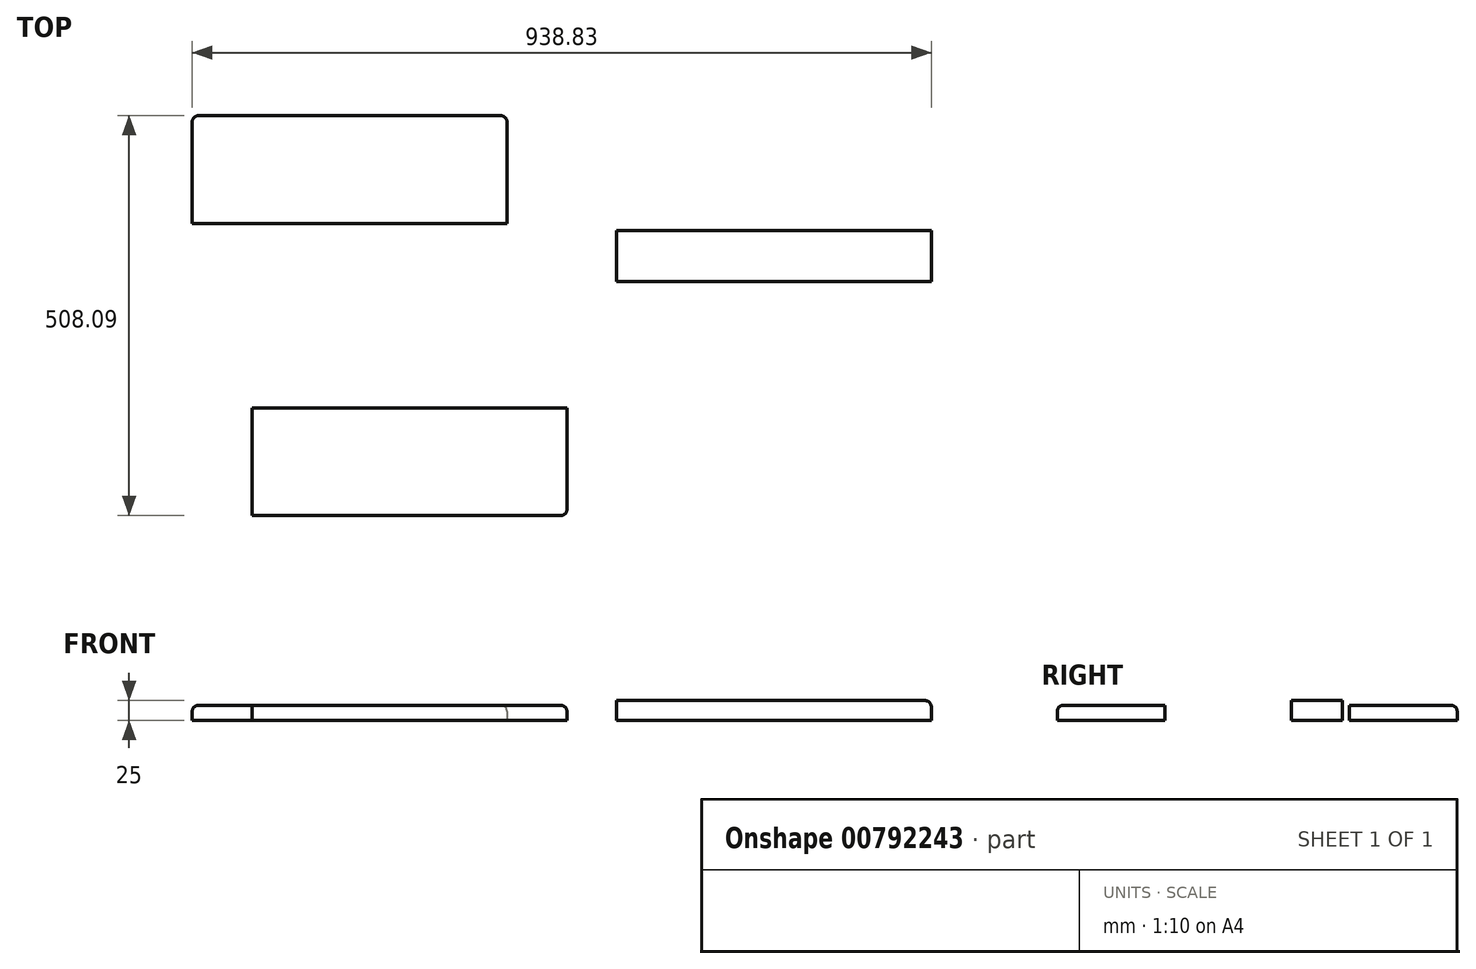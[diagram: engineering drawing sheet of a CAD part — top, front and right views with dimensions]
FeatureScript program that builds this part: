
annotation { "Feature Type Name" : "Feature", "Feature Type Description" : "" }
export const myFeature = defineFeature(function(context is Context, id is Id, definition is map)
    precondition{}
    {
        {
            var Q0;
            Q0=qCreatedBy(makeId("Top.planeOp"),FACE);
            var sketch = newSketch(context, id + "F0", { "sketchPlane" : qUnion([Q0])});
            skLineSegment(sketch, "E0.bottom", {"start": v(0.43, 41.34) * mm, "end": v(-399.57, 41.34) * mm});
            skLineSegment(sketch, "E0.top", {"start": v(0.43, 178.34) * mm, "end": v(-399.57, 178.34) * mm});
            skLineSegment(sketch, "E0.left", {"start": v(0.43, 41.34) * mm, "end": v(0.43, 178.34) * mm});
            skLineSegment(sketch, "E0.right", {"start": v(-399.57, 41.34) * mm, "end": v(-399.57, 178.34) * mm});
            skPoint(sketch, "E0.middle", {"position": v(-199.57, 109.84) * mm});
            skSolve(sketch);
        }
        {
            var Q0;
            Q0=qCreatedBy(makeId("Top.planeOp"),FACE);
            var sketch = newSketch(context, id + "F1", { "sketchPlane" : qUnion([Q0])});
            skLineSegment(sketch, "E1.bottom", {"start": v(76.53, -329.75) * mm, "end": v(-323.47, -329.75) * mm});
            skLineSegment(sketch, "E1.top", {"start": v(76.53, -192.75) * mm, "end": v(-323.47, -192.75) * mm});
            skLineSegment(sketch, "E1.left", {"start": v(76.53, -329.75) * mm, "end": v(76.53, -192.75) * mm});
            skLineSegment(sketch, "E1.right", {"start": v(-323.47, -329.75) * mm, "end": v(-323.47, -192.75) * mm});
            skPoint(sketch, "E1.middle", {"position": v(-123.47, -261.25) * mm});
            skSolve(sketch);
        }
        {
            var Q0;
            Q0=qCreatedBy(makeId("Top.planeOp"),FACE);
            var sketch = newSketch(context, id + "F2", { "sketchPlane" : qUnion([Q0])});
            skLineSegment(sketch, "E2.bottom", {"start": v(539.26, 32.5) * mm, "end": v(139.26, 32.5) * mm});
            skLineSegment(sketch, "E2.top", {"start": v(539.26, -32.5) * mm, "end": v(139.26, -32.5) * mm});
            skLineSegment(sketch, "E2.left", {"start": v(539.26, 32.5) * mm, "end": v(539.26, -32.5) * mm});
            skLineSegment(sketch, "E2.right", {"start": v(139.26, 32.5) * mm, "end": v(139.26, -32.5) * mm});
            skPoint(sketch, "E2.middle", {"position": v(339.26, 0) * mm});
            skSolve(sketch);
        }
        {
            var Q0;
            Q0=makeQuery(id+"F0.imprint","IMPRINT",FACE,{"disambiguationData":[TD([[makeQuery(id+"F0.imprint","IMPRINT",EDGE,{"derivedFrom":sQuery(id+"F0.wireOp",EDGE,"E0.bottom")}),-1.0]])]});
            extrude(context, id + "F3", {"entities" : qUnion([Q0]), "depth" : 19 * mm, "offsetDistance" : 25 * mm});
        }
        {
            var Q0;
            Q0=makeQuery(id+"F1.imprint","IMPRINT",FACE,{"disambiguationData":[TD([[makeQuery(id+"F1.imprint","IMPRINT",EDGE,{"derivedFrom":sQuery(id+"F1.wireOp",EDGE,"E1.bottom")}),-1.0]])]});
            extrude(context, id + "F4", {"entities" : qUnion([Q0]), "depth" : 19 * mm, "offsetDistance" : 25 * mm});
        }
        {
            var Q0;
            Q0=makeQuery(id+"F2.imprint","IMPRINT",FACE,{"disambiguationData":[TD([[makeQuery(id+"F2.imprint","IMPRINT",EDGE,{"derivedFrom":sQuery(id+"F2.wireOp",EDGE,"E2.bottom")}),1.0]])]});
            extrude(context, id + "F5", {"entities" : qUnion([Q0]), "depth" : 25 * mm, "offsetDistance" : 25 * mm});
        }
        {
            var Q0;
            Q0=makeQuery(id+"F3.opExtrude","CAP_EDGE",EDGE,{"disambiguationData":[OSD([sQuery(id+"F0.wireOp",EDGE,"E0.left")])],"isStart":false});
            fillet(context, id + "F6", {"entities" : qUnion([Q0]), "radius" : 8 * mm, "tangentPropagation" : true, "allowEdgeOverflow" : false});
        }
        {
            var Q0;
            Q0=makeQuery(id+"F5.opExtrude","CAP_EDGE",EDGE,{"disambiguationData":[OSD([sQuery(id+"F2.wireOp",EDGE,"E2.left")])],"isStart":false});
            fillet(context, id + "F7", {"entities" : qUnion([Q0]), "radius" : 8 * mm, "tangentPropagation" : true, "allowEdgeOverflow" : false});
        }
        {
            var Q0;
            Q0=makeQuery(id+"F4.opExtrude","CAP_EDGE",EDGE,{"disambiguationData":[OSD([sQuery(id+"F1.wireOp",EDGE,"E1.left")])],"isStart":false});
            fillet(context, id + "F8", {"entities" : qUnion([Q0]), "radius" : 8 * mm, "tangentPropagation" : true, "allowEdgeOverflow" : false});
        }
        {
            var Q0;
            Q0=makeQuery(id+"F4.opExtrude","CAP_EDGE",EDGE,{"disambiguationData":[OSD([sQuery(id+"F1.wireOp",EDGE,"E1.bottom")])],"isStart":false});
            fillet(context, id + "F9", {"entities" : qUnion([Q0]), "radius" : 8 * mm, "tangentPropagation" : true, "allowEdgeOverflow" : false});
        }
        {
            var Q0;
            Q0=makeQuery(id+"F3.opExtrude","CAP_EDGE",EDGE,{"disambiguationData":[OSD([sQuery(id+"F0.wireOp",EDGE,"E0.top")])],"isStart":false});
            fillet(context, id + "F10", {"entities" : qUnion([Q0]), "radius" : 8 * mm, "tangentPropagation" : true, "allowEdgeOverflow" : false});
        }
        {
            var Q0;
            Q0=makeQuery(id+"F3.opExtrude","CAP_EDGE",EDGE,{"disambiguationData":[OSD([sQuery(id+"F0.wireOp",EDGE,"E0.right")])],"isStart":false});
            fillet(context, id + "F11", {"entities" : qUnion([Q0]), "radius" : 8 * mm, "tangentPropagation" : true, "allowEdgeOverflow" : false});
        }
    });
